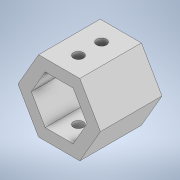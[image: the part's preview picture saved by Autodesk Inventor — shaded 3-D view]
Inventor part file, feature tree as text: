
AUTODESK INVENTOR PART (.ipt)
format: ipt  version: 2022 (Build 260153000, 153)  size: 130,048 bytes
history: native  units: mm
features: extrude x2, sketch x2, projected_geometry x1
ambient origin geometry x8: Origin, YZ Plane, XZ Plane, XY Plane, X Axis, Y Axis, Z Axis, Center Point
bodies: Body1 (feature_tree)
feature tree (5):
  extrude  "Extrusion3"  Depth=60.0mm TaperAngle=360.0deg
  extrude  "Extrusion4"  Depth=1.5mm
  sketch  "Sketch4"  dims[d8=6.2mm d9=60.0mm d11=360.0deg]
  sketch  "Sketch5"  dims[d13=0.45mm d14=1.5mm d15=8.0mm d16=0.0mm d17=1.3mm d18=2.5mm d19=2.5mm d20=10.0mm d21=0.0mm d22=0.5mm d23=0.872665mm]
  projected_geometry  "Projected Loop2"
